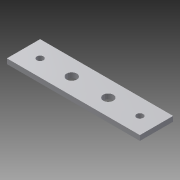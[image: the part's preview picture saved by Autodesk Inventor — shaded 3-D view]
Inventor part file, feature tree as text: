
AUTODESK INVENTOR PART (.ipt)
format: ipt  version: 2015 (Build 190159000, 159)  size: 111,104 bytes
history: native  units: mm
features: sketch x3, hole x2, other x1, extrude x1
ambient origin geometry x8: Origin, YZ Plane, XZ Plane, XY Plane, X Axis, Y Axis, Z Axis, Center Point
bodies: Body1 (feature_tree)
feature tree (7):
  other  "ソリッド1"
  extrude  "押し出し1"  Depth=40.0mm
  hole  "穴1"  [1 undecoded]
  hole  "穴2"  [1 undecoded]
  sketch  "スケッチ1"
  sketch  "スケッチ2"
  sketch  "スケッチ3"
note: 2 required parameter values undecoded (feature->parameter linkage not recoverable at this tier; creation-order binding heuristic only, values carry confidence <= 0.55)
